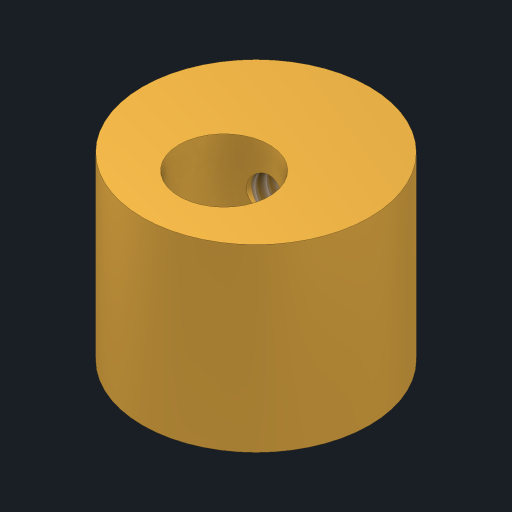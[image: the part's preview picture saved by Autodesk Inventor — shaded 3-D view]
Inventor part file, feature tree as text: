
AUTODESK INVENTOR PART (.ipt)
format: ipt  version: 2023.1 (Build 271208000, 208)  size: 150,528 bytes
history: native  units: mm
features: sketch x2, extrude x1, plane x1, hole x1
ambient origin geometry x8: Origin, YZ Plane, XZ Plane, XY Plane, X Axis, Y Axis, Z Axis, Center Point
bodies: Solid1 (feature_tree)
feature tree (5):
  extrude  "Extrusion1"  Depth=2.25mm
  plane  "Work Plane1"
  hole  "Hole1"  [1 undecoded]
  sketch  "Sketch1"  dims[d5=6.35mm d6=2.25mm]
  sketch  "Sketch2"  dims[d9=9.525mm d11=16.0mm d12=12.7mm d13=0.0mm d14=3.4544mm d15=3.4544mm d16=3.175mm d17=3.175mm d18=2.6416mm d19=7.01mm d20=12.6mm d21=2.0mm d22=90.0deg d23=8.0mm d24=20.594885mm]
note: 1 required parameter value undecoded (feature->parameter linkage not recoverable at this tier; creation-order binding heuristic only, values carry confidence <= 0.55)
